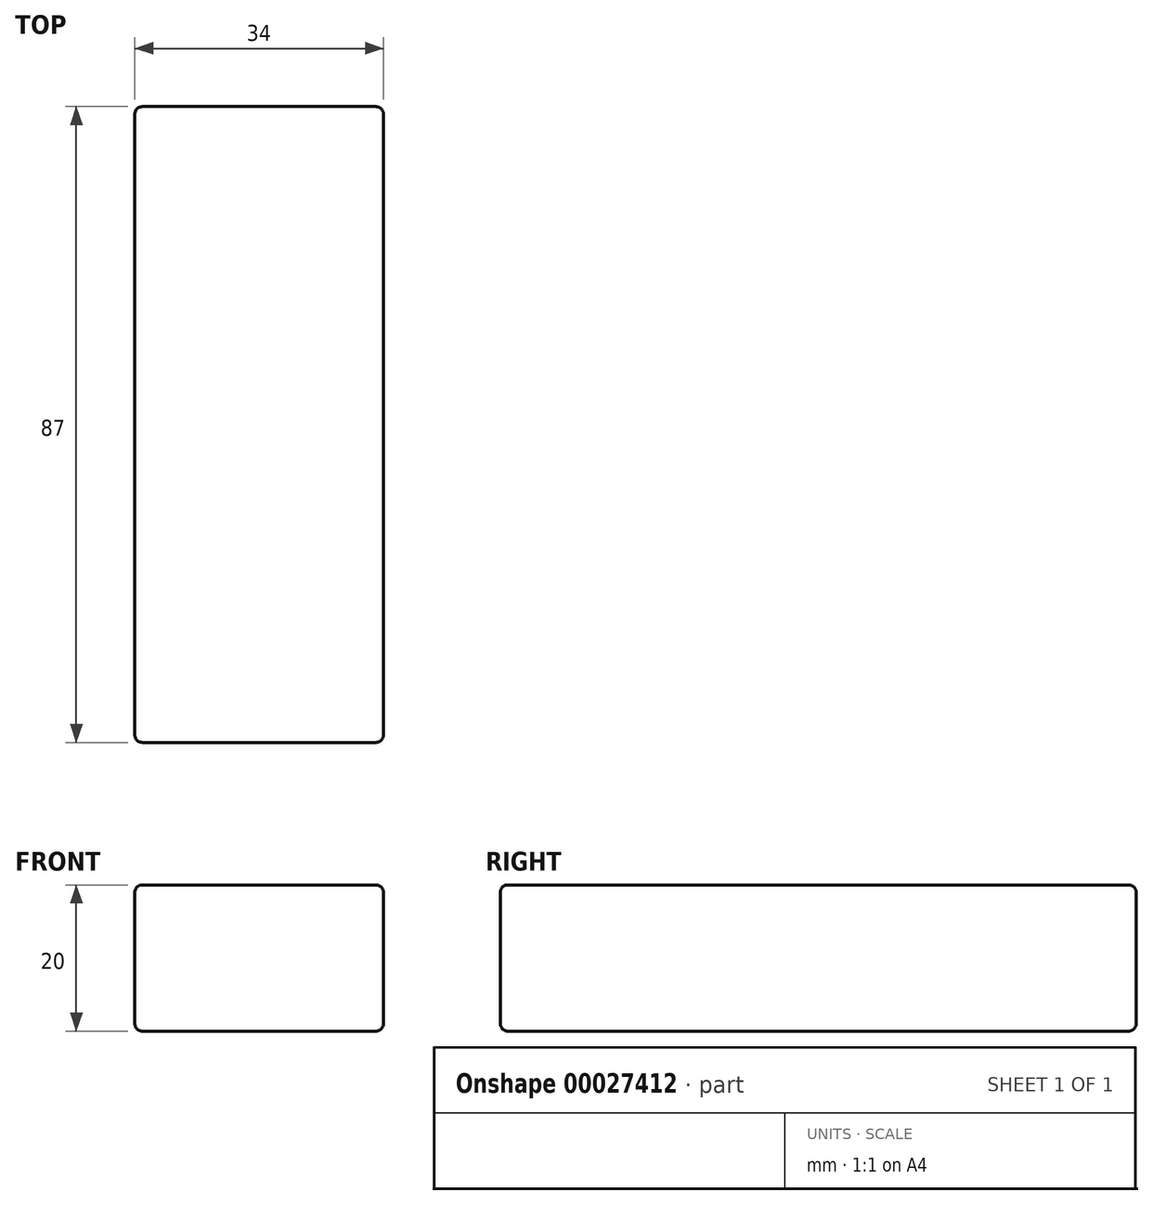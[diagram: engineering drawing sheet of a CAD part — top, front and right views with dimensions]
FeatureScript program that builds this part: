
annotation { "Feature Type Name" : "Feature", "Feature Type Description" : "" }
export const myFeature = defineFeature(function(context is Context, id is Id, definition is map)
    precondition{}
    {
        {
            var Q0;
            Q0=qCreatedBy(makeId("Front.planeOp"),FACE);
            var sketch = newSketch(context, id + "F0", { "sketchPlane" : qUnion([Q0])});
            skLineSegment(sketch, "E0.rect.bottom", {"start": v(17, -10) * mm, "end": v(-17, -10) * mm});
            skLineSegment(sketch, "E0.rect.top", {"start": v(17, 10) * mm, "end": v(-17, 10) * mm});
            skLineSegment(sketch, "E0.rect.left", {"start": v(17, -10) * mm, "end": v(17, 10) * mm});
            skLineSegment(sketch, "E0.rect.right", {"start": v(-17, -10) * mm, "end": v(-17, 10) * mm});
            skPoint(sketch, "E0.rect.middle", {"position": v(0, 0) * mm});
            skSolve(sketch);
        }
        {
            var Q0;
            Q0=makeQuery(id+"F0.imprint","IMPRINT",FACE,{"disambiguationData":[TD([[makeQuery(id+"F0.imprint","IMPRINT",EDGE,{"derivedFrom":sQuery(id+"F0.wireOp",EDGE,"E0.rect.bottom")}),-1.0]])]});
            extrude(context, id + "F1", {"entities" : qUnion([Q0]), "depth" : 87 * mm});
        }
        {
            var Q0;
            Q0=makeQuery(id+"F1.opExtrude","SWEPT_EDGE",EDGE,{"disambiguationData":[OSD([sQuery(id+"F0.wireOp",EDGE,"E0.rect.top"),sQuery(id+"F0.wireOp",EDGE,"E0.rect.right")])]});
            var Q1;
            Q1=makeQuery(id+"F1.opExtrude","SWEPT_EDGE",EDGE,{"disambiguationData":[OSD([sQuery(id+"F0.wireOp",EDGE,"E0.rect.bottom"),sQuery(id+"F0.wireOp",EDGE,"E0.rect.right")])]});
            var Q2;
            Q2=makeQuery(id+"F1.opExtrude","CAP_EDGE",EDGE,{"disambiguationData":[OSD([sQuery(id+"F0.wireOp",EDGE,"E0.rect.right")])],"isStart":true});
            var Q3;
            Q3=makeQuery(id+"F1.opExtrude","CAP_EDGE",EDGE,{"disambiguationData":[OSD([sQuery(id+"F0.wireOp",EDGE,"E0.rect.bottom")])],"isStart":true});
            var Q4;
            Q4=makeQuery(id+"F1.opExtrude","CAP_EDGE",EDGE,{"disambiguationData":[OSD([sQuery(id+"F0.wireOp",EDGE,"E0.rect.left")])],"isStart":true});
            var Q5;
            Q5=makeQuery(id+"F1.opExtrude","CAP_EDGE",EDGE,{"disambiguationData":[OSD([sQuery(id+"F0.wireOp",EDGE,"E0.rect.top")])],"isStart":true});
            var Q6;
            Q6=makeQuery(id+"F1.opExtrude","SWEPT_EDGE",EDGE,{"disambiguationData":[OSD([sQuery(id+"F0.wireOp",EDGE,"E0.rect.top"),sQuery(id+"F0.wireOp",EDGE,"E0.rect.left")])]});
            var Q7;
            Q7=makeQuery(id+"F1.opExtrude","CAP_EDGE",EDGE,{"disambiguationData":[OSD([sQuery(id+"F0.wireOp",EDGE,"E0.rect.top")])],"isStart":false});
            var Q8;
            Q8=makeQuery(id+"F1.opExtrude","CAP_EDGE",EDGE,{"disambiguationData":[OSD([sQuery(id+"F0.wireOp",EDGE,"E0.rect.right")])],"isStart":false});
            var Q9;
            Q9=makeQuery(id+"F1.opExtrude","SWEPT_EDGE",EDGE,{"disambiguationData":[OSD([sQuery(id+"F0.wireOp",EDGE,"E0.rect.bottom"),sQuery(id+"F0.wireOp",EDGE,"E0.rect.left")])]});
            var Q10;
            Q10=makeQuery(id+"F1.opExtrude","CAP_EDGE",EDGE,{"disambiguationData":[OSD([sQuery(id+"F0.wireOp",EDGE,"E0.rect.left")])],"isStart":false});
            var Q11;
            Q11=makeQuery(id+"F1.opExtrude","CAP_EDGE",EDGE,{"disambiguationData":[OSD([sQuery(id+"F0.wireOp",EDGE,"E0.rect.bottom")])],"isStart":false});
            fillet(context, id + "F2", {"entities" : qUnion([Q0, Q1, Q2, Q3, Q4, Q5, Q6, Q7, Q8, Q9, Q10, Q11]), "radius" : 1 * mm, "tangentPropagation" : true, "allowEdgeOverflow" : false});
        }
    });
